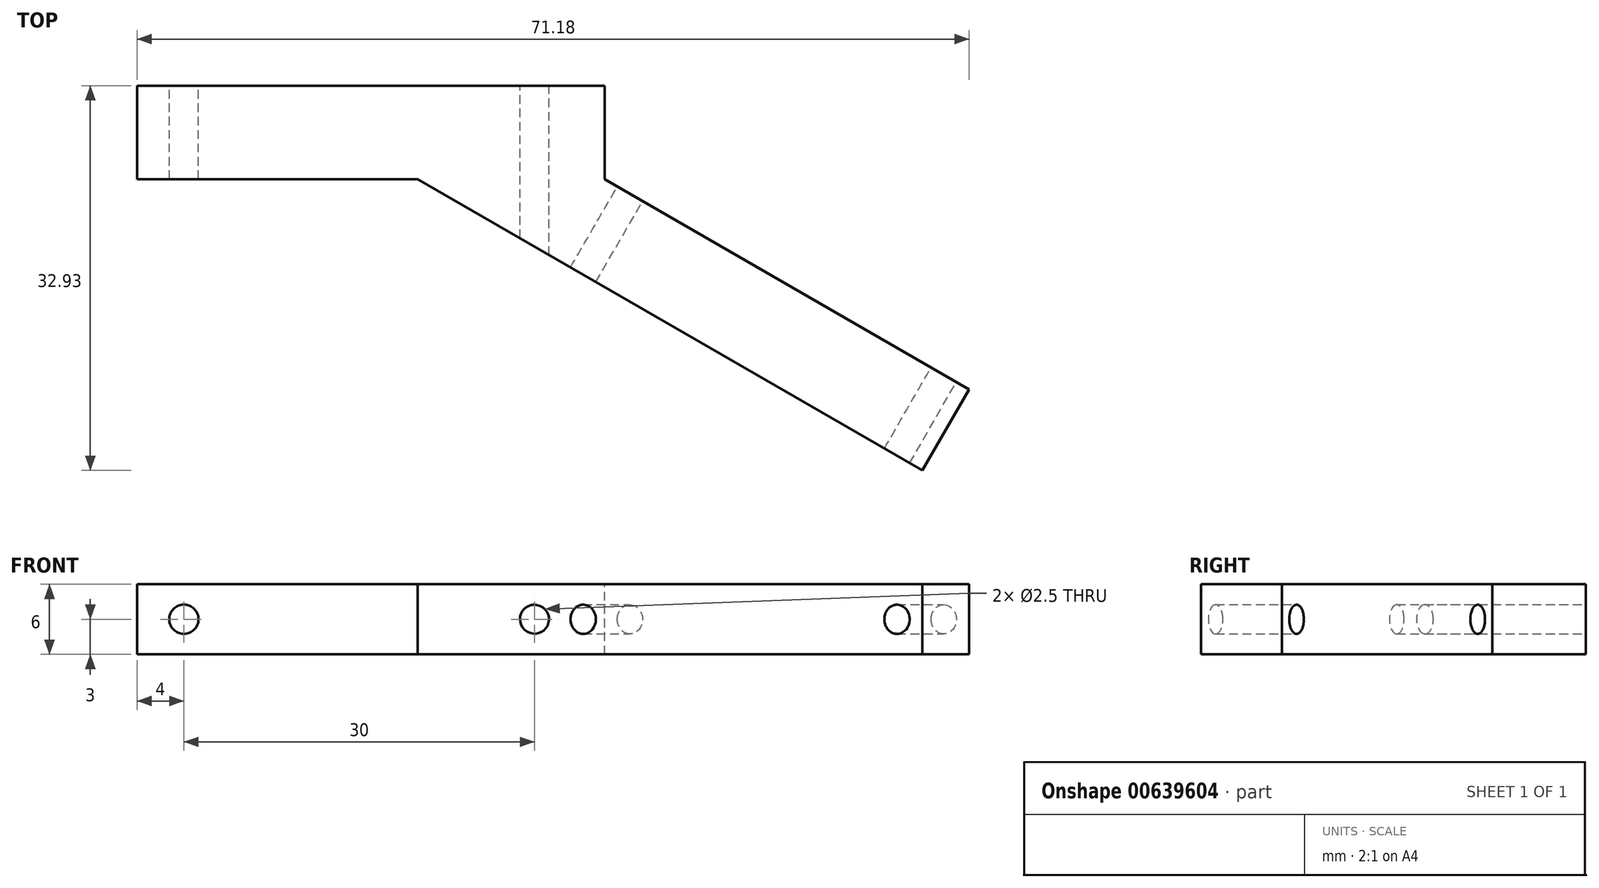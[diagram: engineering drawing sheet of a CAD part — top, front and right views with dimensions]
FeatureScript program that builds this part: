
annotation { "Feature Type Name" : "Feature", "Feature Type Description" : "" }
export const myFeature = defineFeature(function(context is Context, id is Id, definition is map)
    precondition{}
    {
        {
            var Q0;
            Q0=qCreatedBy(makeId("Top.planeOp"),FACE);
            var sketch = newSketch(context, id + "F0", { "sketchPlane" : qUnion([Q0])});
            skLineSegment(sketch, "E0.bottom", {"start": v(0, 0) * mm, "end": v(-40, 0) * mm});
            skLineSegment(sketch, "E0.top", {"start": v(0, 8) * mm, "end": v(-40, 8) * mm});
            skLineSegment(sketch, "E0.left", {"start": v(0, 0) * mm, "end": v(0, 8) * mm});
            skLineSegment(sketch, "E0.right", {"start": v(-40, 0) * mm, "end": v(-40, 8) * mm});
            skLineSegment(sketch, "E1", {"start": v(0, 0) * mm, "end": v(31.18, -18) * mm});
            skLineSegment(sketch, "E2", {"start": v(31.18, -18) * mm, "end": v(27.18, -24.93) * mm});
            skLineSegment(sketch, "E3", {"start": v(27.18, -24.93) * mm, "end": v(-16, 0) * mm});
            skSolve(sketch);
        }
        {
            var Q0;
            Q0=makeQuery(id+"F0.imprint","IMPRINT",FACE,{"disambiguationData":[TD([[makeQuery(id+"F0.imprint","IMPRINT",EDGE,{"derivedFrom":sQuery(id+"F0.wireOp",EDGE,"E0.top")}),1.0]])]});
            var Q1;
            {var subQ0=sQuery(id+"F0.wireOp",EDGE,"E1");Q1=makeQuery(id+"F0.imprint","IMPRINT",FACE,{"disambiguationData":[TD([[makeQuery(id+"F0.imprint","IMPRINT",EDGE,{"derivedFrom":subQ0}),-1.0]])]});}
            extrude(context, id + "F1", {"entities" : qUnion([Q0, Q1]), "oppositeDirection" : true, "depth" : 6 * mm, "offsetDistance" : 25 * mm});
        }
        {
            var Q0;
            Q0=makeQuery(id+"F1.opExtrude","SWEPT_FACE",FACE,{"disambiguationData":[OSD([sQuery(id+"F0.wireOp",EDGE,"E0.top")])]});
            var sketch = newSketch(context, id + "F2", { "sketchPlane" : qUnion([Q0])});
            skPoint(sketch, "E4", {"position": v(36, -3) * mm});
            skPoint(sketch, "E5", {"position": v(6, -3) * mm});
            skSolve(sketch);
        }
        {
            var Q0;
            Q0=makeQuery(id+"F1.opExtrude","SWEPT_FACE",FACE,{"disambiguationData":[OSD([sQuery(id+"F0.wireOp",EDGE,"E1")])]});
            var sketch = newSketch(context, id + "F3", { "sketchPlane" : qUnion([Q0])});
            skPoint(sketch, "E6", {"position": v(-2.5, -3) * mm});
            skPoint(sketch, "E7", {"position": v(-33.5, -3) * mm});
            skSolve(sketch);
        }
        {
            var Q0;
            Q0=sQuery(id+"F3.wireOp",VERTEX,"E7");
            var Q1;
            Q1=sQuery(id+"F3.wireOp",VERTEX,"E6");
            var Q2;
            Q2=sQuery(id+"F2.wireOp",VERTEX,"E5");
            var Q3;
            Q3=sQuery(id+"F2.wireOp",VERTEX,"E4");
            var Q4;
            Q4=makeQuery(id+"F1.opExtrude","SWEPT_BODY",BODY,{"disambiguationData":[OSD([sQuery(id+"F0.wireOp",EDGE,"E0.bottom"),sQuery(id+"F0.wireOp",EDGE,"E0.top"),sQuery(id+"F0.wireOp",EDGE,"E0.left"),sQuery(id+"F0.wireOp",EDGE,"E0.right"),sQuery(id+"F0.wireOp",EDGE,"E1"),sQuery(id+"F0.wireOp",EDGE,"E2"),sQuery(id+"F0.wireOp",EDGE,"E3")])]});
            hole(context, id + "F4", {"style" : HoleStyle.SIMPLE, "endStyle" : HoleEndStyle.THROUGH, "holeDiameter" : 2.5 * mm, "majorDiameter" : 5 * mm, "isTappedThrough" : true, "tappedDepth" : 12 * mm, "tapClearance" : 3, "locations" : qUnion([Q0, Q1, Q2, Q3]), "scope" : qUnion([Q4])});
        }
    });
